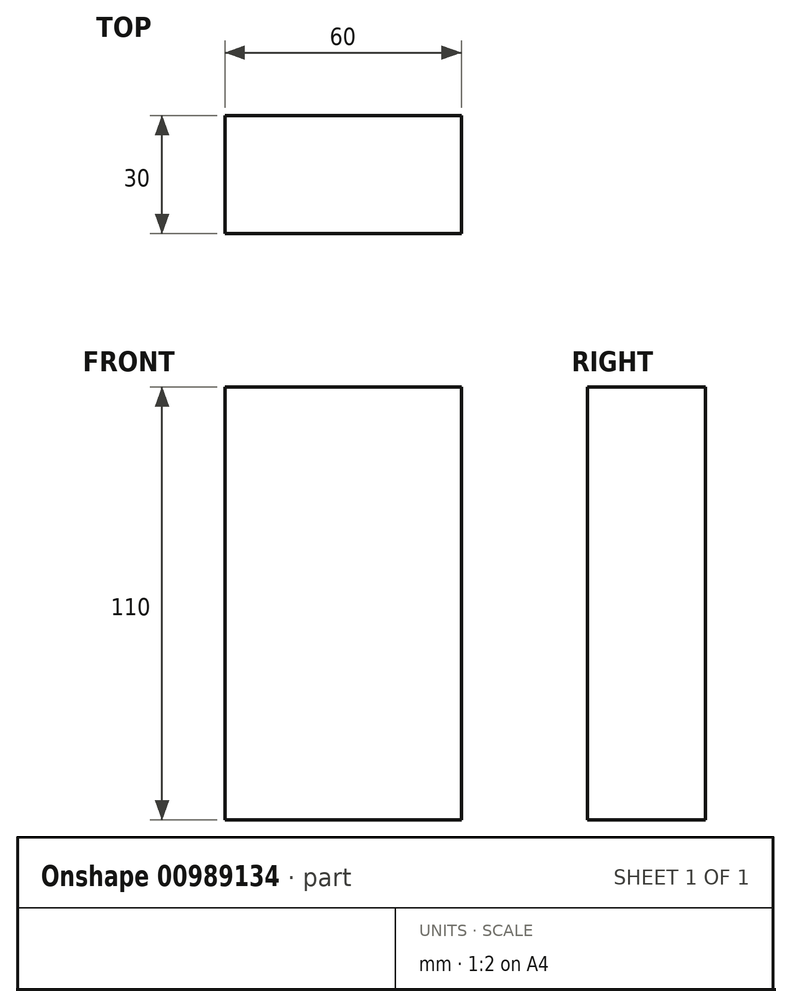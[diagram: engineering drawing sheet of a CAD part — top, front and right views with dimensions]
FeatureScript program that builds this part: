
annotation { "Feature Type Name" : "Feature", "Feature Type Description" : "" }
export const myFeature = defineFeature(function(context is Context, id is Id, definition is map)
    precondition{}
    {
        {
            var Q0;
            Q0=qCreatedBy(makeId("Front.planeOp"),FACE);
            var sketch = newSketch(context, id + "F0", { "sketchPlane" : qUnion([Q0])});
            skLineSegment(sketch, "E0.bottom", {"start": v(30, 55) * mm, "end": v(-30, 55) * mm});
            skLineSegment(sketch, "E0.top", {"start": v(30, -55) * mm, "end": v(-30, -55) * mm});
            skLineSegment(sketch, "E0.left", {"start": v(30, 55) * mm, "end": v(30, -55) * mm});
            skLineSegment(sketch, "E0.right", {"start": v(-30, 55) * mm, "end": v(-30, -55) * mm});
            skPoint(sketch, "E0.middle", {"position": v(0, 0) * mm});
            skSolve(sketch);
        }
        {
            var Q0;
            Q0 = qSketchRegion(id + "F0", true);
            extrude(context, id + "F1", {"entities" : qUnion([Q0]), "depth" : 30 * mm, "offsetDistance" : 25.4 * mm});
        }
    });
